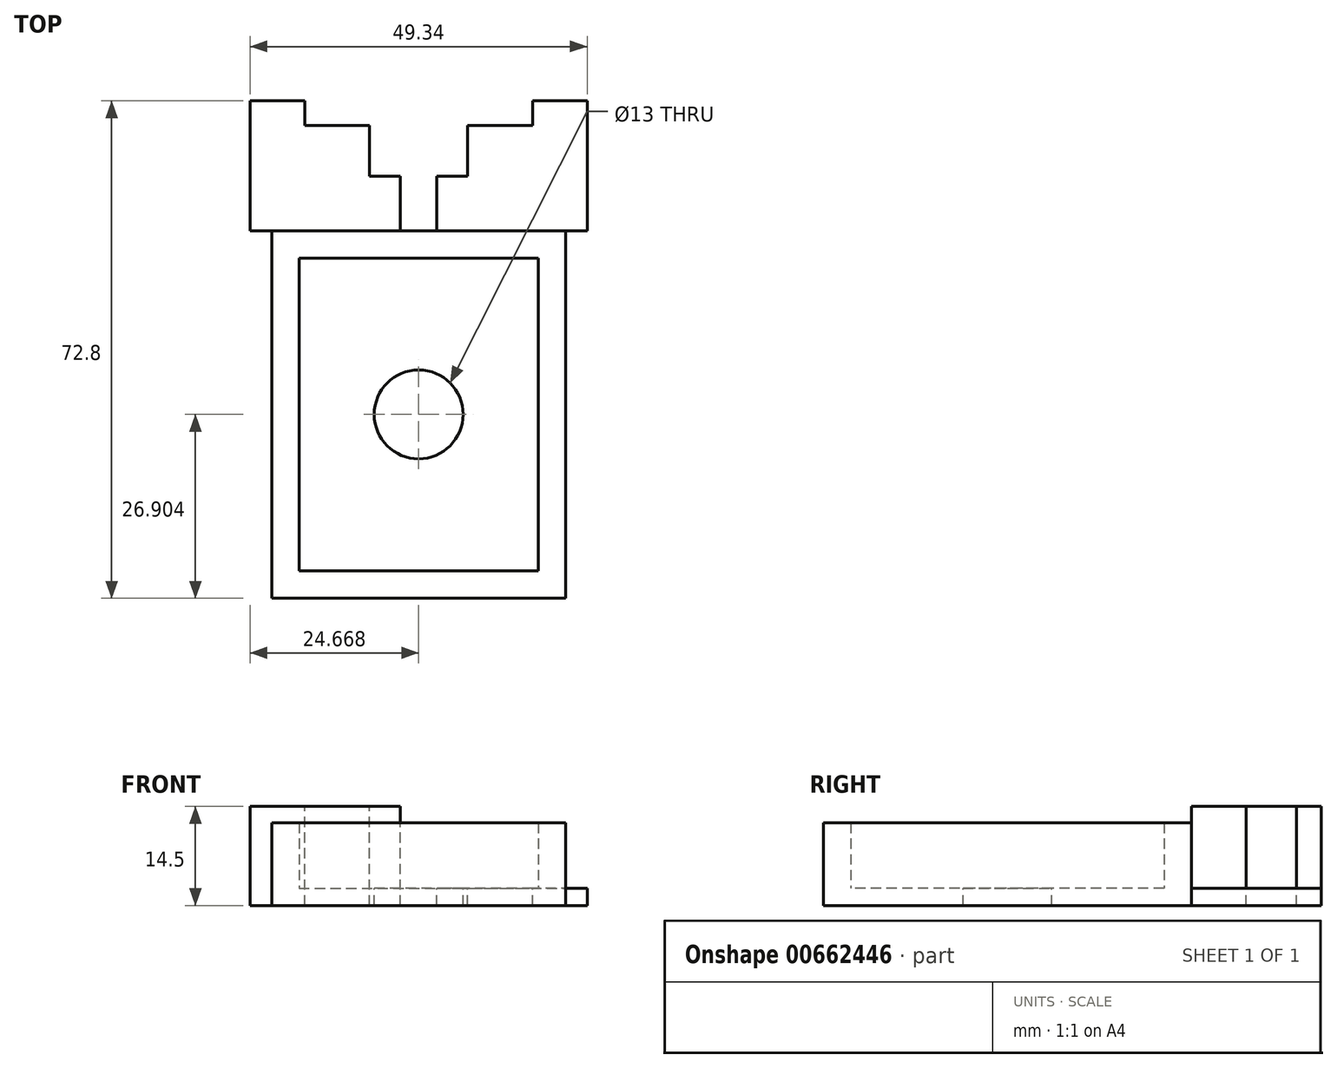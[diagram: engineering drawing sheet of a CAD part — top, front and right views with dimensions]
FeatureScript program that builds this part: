
annotation { "Feature Type Name" : "Feature", "Feature Type Description" : "" }
export const myFeature = defineFeature(function(context is Context, id is Id, definition is map)
    precondition{}
    {
        {
            var Q0;
            Q0=qCreatedBy(makeId("Top.planeOp"),FACE);
            var sketch = newSketch(context, id + "F0", { "sketchPlane" : qUnion([Q0])});
            skLineSegment(sketch, "E0.bottom", {"start": v(-23.45, 23.4) * mm, "end": v(-5.95, 23.4) * mm});
            skLineSegment(sketch, "E0.top", {"start": v(-23.45, -22.4) * mm, "end": v(-5.95, -22.4) * mm});
            skLineSegment(sketch, "E0.left", {"start": v(-23.45, 23.4) * mm, "end": v(-23.45, -22.4) * mm});
            skLineSegment(sketch, "E0.right", {"start": v(11.55, 23.4) * mm, "end": v(11.55, -22.4) * mm});
            skPoint(sketch, "E1", {"position": v(-5.95, 23.4) * mm});
            skLineSegment(sketch, "E2", {"start": v(-5.95, 44.4) * mm, "end": v(-5.95, -51.5) * mm, "construction": true});
            skPoint(sketch, "E3", {"position": v(-5.95, -22.4) * mm});
            skLineSegment(sketch, "E4", {"start": v(-5.95, -22.4) * mm, "end": v(11.55, -22.4) * mm});
            skLineSegment(sketch, "E5", {"start": v(-5.95, 23.4) * mm, "end": v(11.55, 23.4) * mm});
            skLineSegment(sketch, "E6.0", {"start": v(-27.45, 27.4) * mm, "end": v(-8.62, 27.4) * mm});
            skLineSegment(sketch, "E6.1", {"start": v(-27.45, 27.4) * mm, "end": v(-27.45, -26.4) * mm});
            skLineSegment(sketch, "E6.2", {"start": v(-27.45, -26.4) * mm, "end": v(-5.85, -26.4) * mm});
            skLineSegment(sketch, "E7.bottom", {"start": v(-30.62, 46.4) * mm, "end": v(-22.62, 46.4) * mm});
            skLineSegment(sketch, "E7.top", {"start": v(-30.62, 27.4) * mm, "end": v(-27.45, 27.4) * mm});
            skLineSegment(sketch, "E7.left", {"start": v(-30.62, 46.4) * mm, "end": v(-30.62, 27.4) * mm});
            skPoint(sketch, "E8", {"position": v(-8.62, 35.4) * mm});
            skPoint(sketch, "E9", {"position": v(-13.12, 35.4) * mm});
            skLineSegment(sketch, "E10", {"start": v(-13.12, 35.4) * mm, "end": v(-8.62, 35.4) * mm});
            skPoint(sketch, "E11", {"position": v(-22.62, 46.4) * mm});
            skLineSegment(sketch, "E12", {"start": v(-22.62, 46.4) * mm, "end": v(-22.62, 42.8) * mm});
            skLineSegment(sketch, "E13", {"start": v(-22.62, 42.8) * mm, "end": v(-13.12, 42.8) * mm});
            skLineSegment(sketch, "E14", {"start": v(-13.12, 42.8) * mm, "end": v(-13.12, 35.4) * mm});
            skLineSegment(sketch, "E15", {"start": v(-8.62, 35.4) * mm, "end": v(-8.62, 27.4) * mm});
            skLineSegment(sketch, "E16.0", {"start": v(-10.12, 38.4) * mm, "end": v(-5.95, 38.4) * mm});
            skLineSegment(sketch, "E16.1", {"start": v(-30.62, 49.4) * mm, "end": v(-19.62, 49.4) * mm});
            skLineSegment(sketch, "E16.2", {"start": v(-19.62, 49.4) * mm, "end": v(-19.62, 45.8) * mm});
            skLineSegment(sketch, "E16.3", {"start": v(-19.62, 45.8) * mm, "end": v(-10.12, 45.8) * mm});
            skLineSegment(sketch, "E16.4", {"start": v(-10.12, 45.8) * mm, "end": v(-10.12, 38.4) * mm});
            skLineSegment(sketch, "E17.MirrorCS", {"start": v(-1.78, 38.4) * mm, "end": v(-5.95, 38.4) * mm});
            skLineSegment(sketch, "E18.MirrorCS", {"start": v(1.22, 35.4) * mm, "end": v(-3.28, 35.4) * mm});
            skLineSegment(sketch, "E19.MirrorCS", {"start": v(7.72, 45.8) * mm, "end": v(-1.78, 45.8) * mm});
            skLineSegment(sketch, "E20.MirrorCS", {"start": v(10.72, 42.8) * mm, "end": v(1.22, 42.8) * mm});
            skLineSegment(sketch, "E21.MirrorCS", {"start": v(18.72, 27.4) * mm, "end": v(15.55, 27.4) * mm});
            skLineSegment(sketch, "E22.MirrorCS", {"start": v(-1.78, 45.8) * mm, "end": v(-1.78, 38.4) * mm});
            skLineSegment(sketch, "E23.MirrorCS", {"start": v(7.72, 49.4) * mm, "end": v(7.72, 45.8) * mm});
            skLineSegment(sketch, "E24.MirrorCS", {"start": v(1.22, 42.8) * mm, "end": v(1.22, 35.4) * mm});
            skLineSegment(sketch, "E25.MirrorCS", {"start": v(10.72, 46.4) * mm, "end": v(10.72, 42.8) * mm});
            skPoint(sketch, "E26.MirrorP", {"position": v(-3.28, 35.4) * mm});
            skLineSegment(sketch, "E27.MirrorCS", {"start": v(18.72, 46.4) * mm, "end": v(10.72, 46.4) * mm});
            skLineSegment(sketch, "E28.MirrorCS", {"start": v(18.72, 49.4) * mm, "end": v(7.72, 49.4) * mm});
            skLineSegment(sketch, "E29.MirrorCS", {"start": v(-3.28, 35.4) * mm, "end": v(-3.28, 27.4) * mm});
            skLineSegment(sketch, "E30.MirrorCS", {"start": v(15.55, 27.4) * mm, "end": v(-3.28, 27.4) * mm});
            skPoint(sketch, "E31.MirrorP", {"position": v(1.22, 35.4) * mm});
            skLineSegment(sketch, "E32.MirrorCS", {"start": v(11.55, 23.4) * mm, "end": v(-5.95, 23.4) * mm});
            skLineSegment(sketch, "E33.MirrorCS", {"start": v(18.72, 46.4) * mm, "end": v(18.72, 27.4) * mm});
            skLineSegment(sketch, "E34.MirrorCS", {"start": v(11.55, -22.4) * mm, "end": v(-5.95, -22.4) * mm});
            skLineSegment(sketch, "E35.MirrorCS", {"start": v(15.55, -26.4) * mm, "end": v(-6.05, -26.4) * mm});
            skLineSegment(sketch, "E36.MirrorCS", {"start": v(15.55, 27.4) * mm, "end": v(15.55, -26.4) * mm});
            skPoint(sketch, "E37.MirrorP", {"position": v(10.72, 46.4) * mm});
            skLineSegment(sketch, "E38", {"start": v(-30.62, 46.4) * mm, "end": v(-30.62, 49.4) * mm});
            skLineSegment(sketch, "E39", {"start": v(18.72, 46.4) * mm, "end": v(18.72, 49.4) * mm});
            skLineSegment(sketch, "E40", {"start": v(11.55, 23.4) * mm, "end": v(-23.45, -22.4) * mm, "construction": true});
            skLineSegment(sketch, "E41", {"start": v(-23.45, 23.4) * mm, "end": v(11.55, -22.4) * mm, "construction": true});
            skPoint(sketch, "E42", {"position": v(-5.95, 0.5) * mm});
            skCircle(sketch, "E43", {"center": v(-5.95, 0.5) * mm, "radius": 6.5 * mm});
            skLineSegment(sketch, "E44", {"start": v(-8.62, 27.4) * mm, "end": v(-8.62, 27.4) * mm});
            skLineSegment(sketch, "E45", {"start": v(-8.62, 27.4) * mm, "end": v(-5.85, 27.4) * mm});
            skPoint(sketch, "E46", {"position": v(-13.12, 37.76) * mm});
            skPoint(sketch, "E47", {"position": v(1.22, 39.1) * mm});
            skLineSegment(sketch, "E48", {"start": v(15.55, 27.4) * mm, "end": v(15.55, 27.4) * mm});
            skLineSegment(sketch, "E49", {"start": v(-3.28, 27.4) * mm, "end": v(-6.05, 27.4) * mm});
            skSolve(sketch);
        }
        {
            var Q0;
            Q0=makeQuery(id+"F0.imprint","IMPRINT",FACE,{"disambiguationData":[TD([[makeQuery(id+"F0.imprint","IMPRINT",EDGE,{"derivedFrom":sQuery(id+"F0.wireOp",EDGE,"E7.bottom")}),-1.0]])]});
            var Q1;
            {var subQ0=sQuery(id+"F0.wireOp",EDGE,"E6.0");Q1=makeQuery(id+"F0.imprint","IMPRINT",FACE,{"disambiguationData":[TD([[makeQuery(id+"F0.imprint","IMPRINT",EDGE,{"derivedFrom":subQ0}),1.0]])]});}
            var Q2;
            Q2=makeQuery(id+"F0.imprint","IMPRINT",FACE,{"disambiguationData":[TD([[makeQuery(id+"F0.imprint","IMPRINT",EDGE,{"derivedFrom":sQuery(id+"F0.wireOp",EDGE,"E18.MirrorCS")}),1.0]])]});
            var Q3;
            Q3=makeQuery(id+"F0.imprint","IMPRINT",FACE,{"disambiguationData":[TD([[makeQuery(id+"F0.imprint","IMPRINT",EDGE,{"derivedFrom":sQuery(id+"F0.wireOp",EDGE,"E0.bottom")}),1.0]])]});
            var Q4;
            Q4=makeQuery(id+"F0.imprint","IMPRINT",FACE,{"disambiguationData":[TD([[makeQuery(id+"F0.imprint","IMPRINT",EDGE,{"derivedFrom":sQuery(id+"F0.wireOp",EDGE,"E0.bottom")}),-1.0]])]});
            extrude(context, id + "F1", {"entities" : qUnion([Q0, Q1, Q2, Q3, Q4]), "oppositeDirection" : true, "depth" : 2.5 * mm, "offsetDistance" : 25 * mm});
        }
        {
            var Q0;
            {var subQ0=sQuery(id+"F0.wireOp",EDGE,"E6.0");Q0=makeQuery(id+"F0.imprint","IMPRINT",FACE,{"disambiguationData":[TD([[makeQuery(id+"F0.imprint","IMPRINT",EDGE,{"derivedFrom":subQ0}),1.0]])]});}
            extrude(context, id + "F2", {"entities" : qUnion([Q0]), "operationType" : NewBodyOperationType.ADD, "depth" : 12 * mm, "offsetDistance" : 25 * mm});
        }
        {
            var Q0;
            Q0=makeQuery(id+"F0.imprint","IMPRINT",FACE,{"disambiguationData":[TD([[makeQuery(id+"F0.imprint","IMPRINT",EDGE,{"derivedFrom":sQuery(id+"F0.wireOp",EDGE,"E0.bottom")}),1.0]])]});
            extrude(context, id + "F3", {"entities" : qUnion([Q0]), "operationType" : NewBodyOperationType.ADD, "depth" : 9.6 * mm, "offsetDistance" : 25 * mm});
        }
    });
